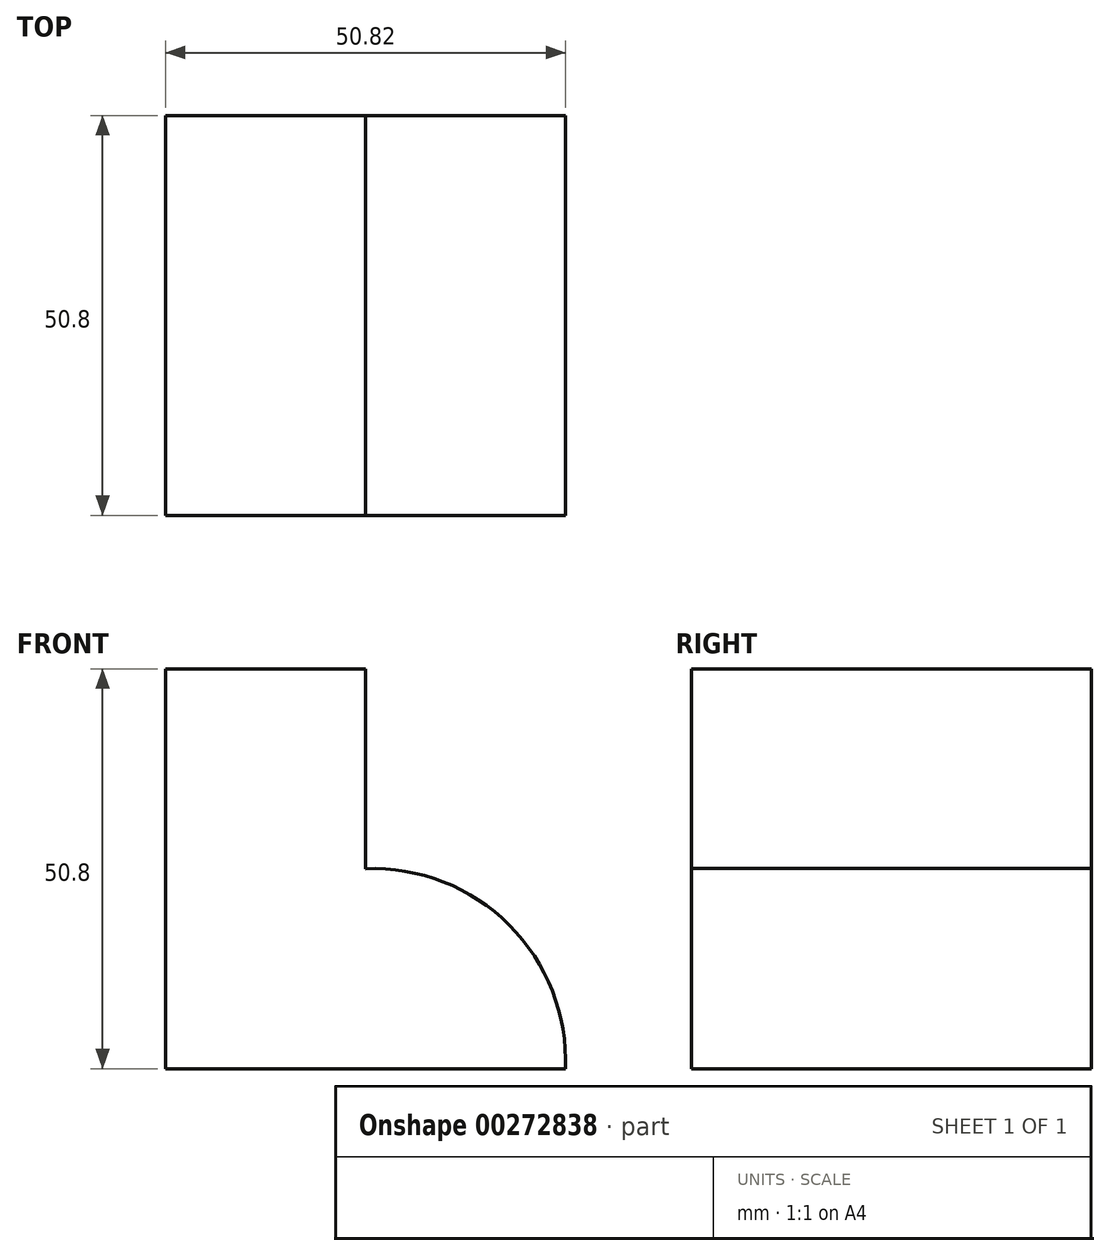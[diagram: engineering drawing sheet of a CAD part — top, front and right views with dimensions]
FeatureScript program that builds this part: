
annotation { "Feature Type Name" : "Feature", "Feature Type Description" : "" }
export const myFeature = defineFeature(function(context is Context, id is Id, definition is map)
    precondition{}
    {
        {
            var Q0;
            Q0=qCreatedBy(makeId("Front.planeOp"),FACE);
            var sketch = newSketch(context, id + "F0", { "sketchPlane" : qUnion([Q0])});
            skLineSegment(sketch, "E0", {"start": v(0, 0) * mm, "end": v(-50.8, 0) * mm});
            skLineSegment(sketch, "E1", {"start": v(-50.8, 0) * mm, "end": v(-50.8, 50.8) * mm});
            skLineSegment(sketch, "E2", {"start": v(-50.8, 50.8) * mm, "end": v(-25.4, 50.8) * mm});
            skLineSegment(sketch, "E3", {"start": v(-25.4, 50.8) * mm, "end": v(-25.4, 25.4) * mm});
            skArc(sketch, "E4", {"start": v(0, 0) * mm, "mid": v(-7.15, 18.25) * mm, "end": v(-25.4, 25.4) * mm});
            skSolve(sketch);
        }
        {
            var Q0;
            Q0=makeQuery(id+"F0.imprint","IMPRINT",FACE,{"disambiguationData":[TD([[makeQuery(id+"F0.imprint","IMPRINT",EDGE,{"derivedFrom":sQuery(id+"F0.wireOp",EDGE,"E0")}),-1.0]])]});
            extrude(context, id + "F1", {"entities" : qUnion([Q0]), "depth" : 50.8 * mm});
        }
    });
